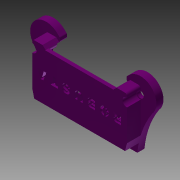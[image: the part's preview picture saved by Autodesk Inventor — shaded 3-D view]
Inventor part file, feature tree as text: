
AUTODESK INVENTOR PART (.ipt)
format: ipt  version: 2015 (Build 190159000, 159)  size: 596,480 bytes
history: native  units: mm
features: sketch x8, extrude x8, projected_geometry x5, plane x3
ambient origin geometry x8: Origin, YZ Plane, XZ Plane, XY Plane, X Axis, Y Axis, Z Axis, Center Point
bodies: Body1 (feature_tree)
feature tree (24):
  plane  "Work Plane2"
  sketch  "Sketch12"  dims[d19=46.65mm d72=0.0mm d125=-8.5mm d129=3.5mm]
  plane  "Work Plane3"
  extrude  "Extrusion9"  Depth=3.5mm
  extrude  "Extrusion10"  Depth=7.0mm TaperAngle=0.0deg
  extrude  "Extrusion11"  Depth=13.5mm TaperAngle=0.0deg
  extrude  "Extrusion12"  Depth=3.5mm TaperAngle=0.0deg
  extrude  "Extrusion13"  Depth=3.5mm TaperAngle=0.0deg
  extrude  "Extrusion14"  Depth=4.46mm
  extrude  "Extrusion15"  Depth=50.0mm TaperAngle=0.0deg
  plane  "Work Plane4"
  extrude  "Extrusion16"  [1 undecoded]
  sketch  "Sketch13"  dims[d136=-5.0mm d137=7.0mm d138=0.0mm]
  sketch  "Sketch14"  dims[d139=3.5mm d140=0.0mm d143=13.5mm d144=0.0mm]
  sketch  "Sketch16"  dims[d145=3.5mm d146=0.0mm d147=3.5mm d148=0.0mm]
  projected_geometry  "Projected Loop1"
  projected_geometry  "Projected Loop2"
  projected_geometry  "Projected Loop3"
  sketch  "Sketch17"  dims[d149=3.5mm d150=0.0mm d158=3.5mm d159=0.0mm]
  sketch  "Sketch18"  dims[d161=0.0mm d162=4.46mm]
  projected_geometry  "Projected Loop4"
  sketch  "Sketch19"  dims[d163=45.0deg d164=50.0mm d165=0.0mm]
  projected_geometry  "Projected Loop6"
  sketch  "Sketch20"
note: 1 required parameter value undecoded (feature->parameter linkage not recoverable at this tier; creation-order binding heuristic only, values carry confidence <= 0.55)
